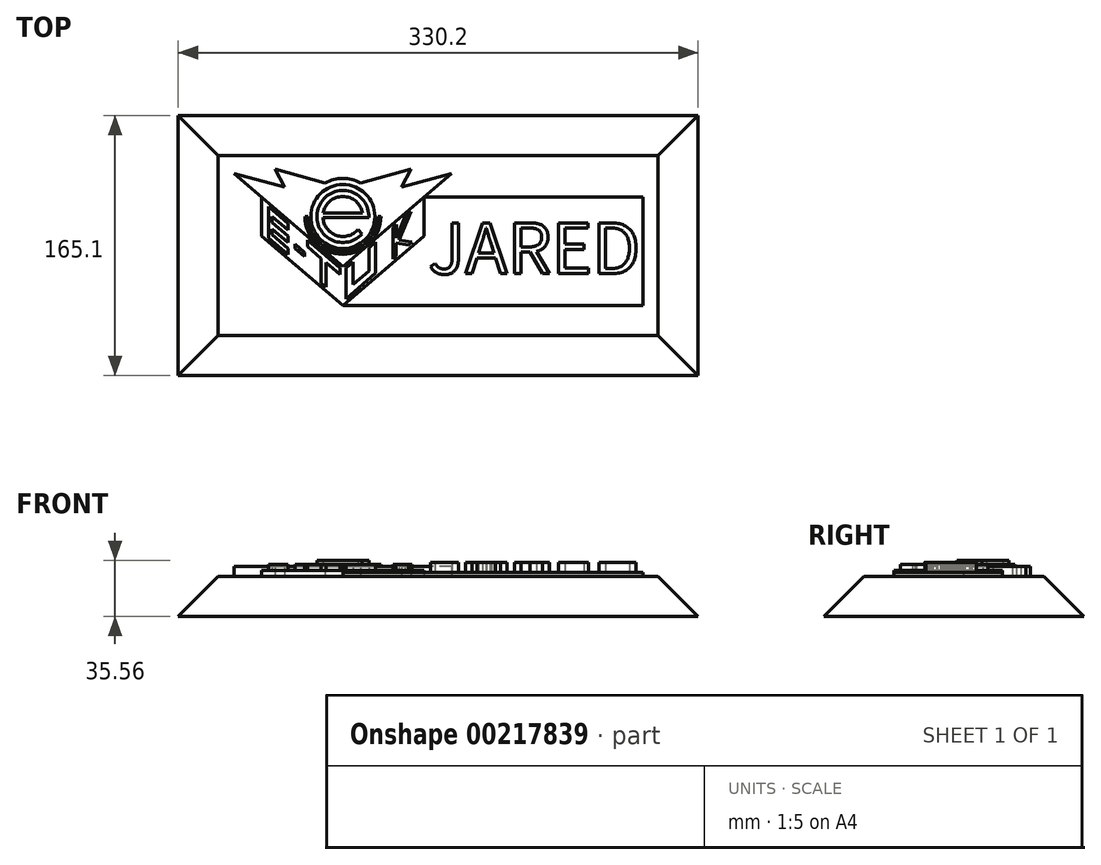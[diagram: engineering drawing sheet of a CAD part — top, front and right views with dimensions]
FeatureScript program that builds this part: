
annotation { "Feature Type Name" : "Feature", "Feature Type Description" : "" }
export const myFeature = defineFeature(function(context is Context, id is Id, definition is map)
    precondition{}
    {
        {
            var Q0;
            Q0=qCreatedBy(makeId("Top.planeOp"),FACE);
            var sketch = newSketch(context, id + "F0", { "sketchPlane" : qUnion([Q0])});
            skArc(sketch, "E0", {"start": v(12.53, 2.07) * mm, "mid": v(0, 12.7) * mm, "end": v(-12.53, 2.07) * mm});
            skArc(sketch, "E1", {"start": v(16.5, -0.78) * mm, "mid": v(-15.23, 6.37) * mm, "end": v(12.14, -11.18) * mm});
            skLineSegment(sketch, "E2", {"start": v(12.7, -0.78) * mm, "end": v(-12.68, -0.78) * mm});
            skLineSegment(sketch, "E3", {"start": v(-12.68, -0.78) * mm, "end": v(16.5, -0.78) * mm});
            skLineSegment(sketch, "E4", {"start": v(9.59, -8.33) * mm, "end": v(12.14, -11.18) * mm});
            skArc(sketch, "E5.trimOffspring", {"start": v(-12.68, -0.78) * mm, "mid": v(-4.08, -12.03) * mm, "end": v(9.59, -8.33) * mm});
            skLineSegment(sketch, "E6", {"start": v(-12.53, 2.07) * mm, "end": v(12.53, 2.07) * mm});
            skSolve(sketch);
        }
        {
            var Q0;
            Q0=makeQuery(id+"F0.imprint","IMPRINT",FACE,{"disambiguationData":[TD([[makeQuery(id+"F0.imprint","IMPRINT",EDGE,{"derivedFrom":sQuery(id+"F0.wireOp",EDGE,"E0")}),-1.0]])]});
            extrude(context, id + "F1", {"entities" : qUnion([Q0]), "depth" : 10.16 * mm});
        }
        {
            var Q0;
            Q0=qCreatedBy(makeId("Top.planeOp"),FACE);
            var sketch = newSketch(context, id + "F2", { "sketchPlane" : qUnion([Q0])});
            skCircle(sketch, "E7", {"center": v(0, 0) * mm, "radius": 20.32 * mm});
            skSolve(sketch);
        }
        {
            var Q0;
            Q0=qSketchRegion(id+"F2",true);
            extrude(context, id + "F3", {"entities" : qUnion([Q0]), "operationType" : NewBodyOperationType.ADD, "depth" : 7.62 * mm});
        }
        {
            var Q0;
            Q0=qCreatedBy(makeId("Top.planeOp"),FACE);
            var sketch = newSketch(context, id + "F4", { "sketchPlane" : qUnion([Q0])});
            skLineSegment(sketch, "E8", {"start": v(-69.02, 27.27) * mm, "end": v(-37.13, 18.72) * mm});
            skLineSegment(sketch, "E9", {"start": v(-37.13, 18.72) * mm, "end": v(-43.14, 30.14) * mm});
            skLineSegment(sketch, "E10", {"start": v(-43.14, 30.14) * mm, "end": v(-11.32, 21.31) * mm});
            skLineSegment(sketch, "E11", {"start": v(-69.02, 27.27) * mm, "end": v(0, -31.75) * mm});
            skLineSegment(sketch, "E12.MirrorCS", {"start": v(43.14, 30.14) * mm, "end": v(11.32, 21.31) * mm});
            skLineSegment(sketch, "E13.MirrorCS", {"start": v(69.02, 27.27) * mm, "end": v(0, -31.75) * mm});
            skLineSegment(sketch, "E14.MirrorCS", {"start": v(69.02, 27.27) * mm, "end": v(37.13, 18.72) * mm});
            skLineSegment(sketch, "E15.MirrorCS", {"start": v(37.13, 18.72) * mm, "end": v(43.14, 30.14) * mm});
            skArc(sketch, "E16.trimOffspring", {"start": v(11.32, 21.31) * mm, "mid": v(0, 24.13) * mm, "end": v(-11.32, 21.31) * mm});
            skSolve(sketch);
        }
        {
            var Q0;
            Q0=qSketchRegion(id+"F4",true);
            var Q1;
            Q1=makeQuery(id+"F2.imprint","IMPRINT",FACE,{"disambiguationData":[TD([[makeQuery(id+"F2.imprint","IMPRINT",EDGE,{"derivedFrom":sQuery(id+"F2.wireOp",EDGE,"E7")}),1.0]])]});
            extrude(context, id + "F5", {"entities" : qUnion([Q0, Q1]), "operationType" : NewBodyOperationType.ADD, "depth" : 6.35 * mm});
        }
        {
            var Q0;
            Q0=qCreatedBy(makeId("Top.planeOp"),FACE);
            var sketch = newSketch(context, id + "F6", { "sketchPlane" : qUnion([Q0])});
            skLineSegment(sketch, "E17", {"start": v(-51.6, -12.38) * mm, "end": v(0, -56.51) * mm});
            skLineSegment(sketch, "E18", {"start": v(0, -56.51) * mm, "end": v(51.6, -12.38) * mm});
            skLineSegment(sketch, "E19", {"start": v(-51.6, 12.38) * mm, "end": v(-51.6, -12.38) * mm});
            skLineSegment(sketch, "E20", {"start": v(51.6, 12.38) * mm, "end": v(51.6, -12.38) * mm});
            skLineSegment(sketch, "E21", {"start": v(-51.6, 12.38) * mm, "end": v(0, -31.75) * mm});
            skLineSegment(sketch, "E22", {"start": v(0, -31.75) * mm, "end": v(51.6, 12.38) * mm});
            skSolve(sketch);
        }
        {
            var Q0;
            Q0=qSketchRegion(id+"F6",true);
            extrude(context, id + "F7", {"entities" : qUnion([Q0]), "operationType" : NewBodyOperationType.ADD, "depth" : 3.8 * mm});
        }
        {
            var Q0;
            Q0=makeQuery(id+"F7.opExtrude","CAP_FACE",FACE,{"disambiguationData":[OSD([sQuery(id+"F6.wireOp",EDGE,"E17"),sQuery(id+"F6.wireOp",EDGE,"E18"),sQuery(id+"F6.wireOp",EDGE,"E19"),sQuery(id+"F6.wireOp",EDGE,"E20"),sQuery(id+"F6.wireOp",EDGE,"E21"),sQuery(id+"F6.wireOp",EDGE,"E22")])],"isStart":false});
            var sketch = newSketch(context, id + "F8", { "sketchPlane" : qUnion([Q0])});
            skPoint(sketch, "E23.startSnap0", {"position": v(-51.6, 0) * mm});
            skLineSegment(sketch, "E24", {"start": v(-51.6, -9.87) * mm, "end": v(-51.6, 9.87) * mm, "construction": true});
            skLineSegment(sketch, "E25", {"start": v(-47.26, 6.16) * mm, "end": v(-34.74, -4.55) * mm});
            skLineSegment(sketch, "E26", {"start": v(-34.74, -4.55) * mm, "end": v(-34.74, -8.63) * mm});
            skLineSegment(sketch, "E27", {"start": v(-34.74, -8.63) * mm, "end": v(-44.83, 0) * mm});
            skLineSegment(sketch, "E28", {"start": v(-44.83, 0) * mm, "end": v(-44.83, -3.75) * mm});
            skLineSegment(sketch, "E29", {"start": v(-44.83, -3.75) * mm, "end": v(-34.74, -12.38) * mm});
            skLineSegment(sketch, "E30", {"start": v(-34.74, -12.38) * mm, "end": v(-34.74, -16.46) * mm});
            skLineSegment(sketch, "E31", {"start": v(-34.74, -16.46) * mm, "end": v(-44.83, -7.83) * mm});
            skLineSegment(sketch, "E32", {"start": v(-44.83, -7.83) * mm, "end": v(-44.83, -11.58) * mm});
            skLineSegment(sketch, "E33", {"start": v(-44.83, -11.58) * mm, "end": v(-34.74, -20.21) * mm});
            skLineSegment(sketch, "E34", {"start": v(-34.74, -20.21) * mm, "end": v(-34.74, -24.3) * mm});
            skLineSegment(sketch, "E35", {"start": v(-34.74, -24.3) * mm, "end": v(-47.26, -13.59) * mm});
            skLineSegment(sketch, "E36", {"start": v(-47.26, 6.16) * mm, "end": v(-47.26, -13.59) * mm});
            skLineSegment(sketch, "E37", {"start": v(-30.38, -20.21) * mm, "end": v(-30.38, -17.65) * mm});
            skLineSegment(sketch, "E38", {"start": v(-30.38, -17.65) * mm, "end": v(-24.17, -22.96) * mm});
            skLineSegment(sketch, "E39", {"start": v(-24.17, -22.96) * mm, "end": v(-24.17, -25.53) * mm});
            skLineSegment(sketch, "E40", {"start": v(-24.17, -25.53) * mm, "end": v(-30.38, -20.21) * mm});
            skLineSegment(sketch, "E41", {"start": v(-22.38, -15.12) * mm, "end": v(-1.9, -32.63) * mm});
            skLineSegment(sketch, "E42", {"start": v(-1.9, -32.63) * mm, "end": v(-1.9, -36.71) * mm});
            skLineSegment(sketch, "E43", {"start": v(-1.9, -36.71) * mm, "end": v(-10.6, -29.28) * mm});
            skLineSegment(sketch, "E44", {"start": v(-10.6, -29.28) * mm, "end": v(-10.6, -44.95) * mm});
            skLineSegment(sketch, "E45", {"start": v(-10.6, -44.95) * mm, "end": v(-13.7, -42.3) * mm});
            skLineSegment(sketch, "E46", {"start": v(-13.7, -42.3) * mm, "end": v(-13.7, -26.63) * mm});
            skLineSegment(sketch, "E47", {"start": v(-13.7, -26.63) * mm, "end": v(-22.38, -19.2) * mm});
            skLineSegment(sketch, "E48", {"start": v(-22.38, -19.2) * mm, "end": v(-22.38, -15.12) * mm});
            skLineSegment(sketch, "E49", {"start": v(1.9, -32.62) * mm, "end": v(6.3, -28.86) * mm});
            skLineSegment(sketch, "E50", {"start": v(6.3, -28.86) * mm, "end": v(6.3, -43.26) * mm});
            skLineSegment(sketch, "E51", {"start": v(6.3, -43.26) * mm, "end": v(16.5, -34.54) * mm});
            skLineSegment(sketch, "E52", {"start": v(16.5, -34.54) * mm, "end": v(16.5, -20.14) * mm});
            skLineSegment(sketch, "E53", {"start": v(16.5, -20.14) * mm, "end": v(20.85, -16.3) * mm});
            skLineSegment(sketch, "E54", {"start": v(20.85, -16.3) * mm, "end": v(20.85, -36.06) * mm});
            skLineSegment(sketch, "E55", {"start": v(20.85, -36.06) * mm, "end": v(1.9, -52.37) * mm});
            skLineSegment(sketch, "E56", {"start": v(1.9, -52.37) * mm, "end": v(1.9, -32.62) * mm});
            skLineSegment(sketch, "E57", {"start": v(31.73, -7.12) * mm, "end": v(31.73, -27.15) * mm});
            skLineSegment(sketch, "E58", {"start": v(31.73, -27.15) * mm, "end": v(33.91, -25.22) * mm});
            skLineSegment(sketch, "E59", {"start": v(33.91, -25.22) * mm, "end": v(33.91, -16.82) * mm});
            skLineSegment(sketch, "E60", {"start": v(33.94, -13.64) * mm, "end": v(33.94, -5.23) * mm});
            skLineSegment(sketch, "E61", {"start": v(33.94, -5.23) * mm, "end": v(31.73, -7.12) * mm});
            skLineSegment(sketch, "E62", {"start": v(41.79, -18.27) * mm, "end": v(44, -16.38) * mm});
            skLineSegment(sketch, "E63", {"start": v(33.94, -13.64) * mm, "end": v(39.5, 0) * mm});
            skLineSegment(sketch, "E64", {"start": v(33.91, -16.82) * mm, "end": v(41.79, -18.27) * mm});
            skLineSegment(sketch, "E65", {"start": v(44, -16.38) * mm, "end": v(35.85, -14.87) * mm});
            skLineSegment(sketch, "E66", {"start": v(35.85, -14.87) * mm, "end": v(43.2, 3.16) * mm});
            skLineSegment(sketch, "E67", {"start": v(39.5, 0) * mm, "end": v(43.2, 3.16) * mm});
            skSolve(sketch);
        }
        {
            var Q0;
            Q0=qSketchRegion(id+"F8",true);
            extrude(context, id + "F9", {"entities" : qUnion([Q0]), "operationType" : NewBodyOperationType.ADD, "depth" : 3.8 * mm});
        }
        {
            var Q0;
            Q0=makeQuery(id+"F5.boolean.opBoolean","MERGE",FACE,{"derivedFrom":[makeQuery(id+"F5.opExtrude","CAP_FACE",FACE,{"disambiguationData":[OSD([sQuery(id+"F2.wireOp",EDGE,"E7")])],"isStart":false}),makeQuery(id+"F5.opExtrude","CAP_FACE",FACE,{"disambiguationData":[OSD([sQuery(id+"F4.wireOp",EDGE,"E8"),sQuery(id+"F4.wireOp",EDGE,"E9"),sQuery(id+"F4.wireOp",EDGE,"E10"),sQuery(id+"F4.wireOp",EDGE,"E11"),sQuery(id+"F4.wireOp",EDGE,"E13.MirrorCS"),sQuery(id+"F4.wireOp",EDGE,"E14.MirrorCS"),sQuery(id+"F4.wireOp",EDGE,"E12.MirrorCS"),sQuery(id+"F4.wireOp",EDGE,"E15.MirrorCS"),sQuery(id+"F4.wireOp",EDGE,"E16.trimOffspring")])],"isStart":false})]});
            var sketch = newSketch(context, id + "F10", { "sketchPlane" : qUnion([Q0])});
            skArc(sketch, "E68", {"start": v(-24.13, 0) * mm, "mid": v(0, -24.13) * mm, "end": v(24.13, 0) * mm});
            skArc(sketch, "E69", {"start": v(-22.23, 0) * mm, "mid": v(0, -22.23) * mm, "end": v(22.23, 0) * mm});
            skLineSegment(sketch, "E70", {"start": v(-24.13, 0) * mm, "end": v(-22.23, 0) * mm});
            skLineSegment(sketch, "E71", {"start": v(24.13, 0) * mm, "end": v(22.23, 0) * mm});
            skSolve(sketch);
        }
        {
            var Q0;
            Q0=qSketchRegion(id+"F10",true);
            extrude(context, id + "F11", {"entities" : qUnion([Q0]), "operationType" : NewBodyOperationType.ADD, "depth" : 1.27 * mm});
        }
        {
            var Q0;
            {var subQ0=sQuery(id+"F2.wireOp",EDGE,"E7");Q0=makeQuery(id+"F7.boolean.opBoolean","MERGE",FACE,{"derivedFrom":[makeQuery(id+"F5.boolean.opBoolean","MERGE",FACE,{"derivedFrom":[makeQuery(id+"F3.boolean.opBoolean","MERGE",FACE,{"derivedFrom":[makeQuery(id+"F1.opExtrude","CAP_FACE",FACE,{"disambiguationData":[OSD([sQuery(id+"F0.wireOp",EDGE,"E0"),sQuery(id+"F0.wireOp",EDGE,"E1"),sQuery(id+"F0.wireOp",EDGE,"E3"),sQuery(id+"F0.wireOp",EDGE,"E4"),sQuery(id+"F0.wireOp",EDGE,"E5.trimOffspring"),sQuery(id+"F0.wireOp",EDGE,"E6")])],"isStart":true}),makeQuery(id+"F3.opExtrude","CAP_FACE",FACE,{"disambiguationData":[OSD([subQ0])],"isStart":true})]}),makeQuery(id+"F5.opExtrude","CAP_FACE",FACE,{"disambiguationData":[OSD([subQ0])],"isStart":true}),makeQuery(id+"F5.opExtrude","CAP_FACE",FACE,{"disambiguationData":[OSD([sQuery(id+"F4.wireOp",EDGE,"E8"),sQuery(id+"F4.wireOp",EDGE,"E9"),sQuery(id+"F4.wireOp",EDGE,"E10"),sQuery(id+"F4.wireOp",EDGE,"E11"),sQuery(id+"F4.wireOp",EDGE,"E13.MirrorCS"),sQuery(id+"F4.wireOp",EDGE,"E14.MirrorCS"),sQuery(id+"F4.wireOp",EDGE,"E12.MirrorCS"),sQuery(id+"F4.wireOp",EDGE,"E15.MirrorCS"),sQuery(id+"F4.wireOp",EDGE,"E16.trimOffspring")])],"isStart":true})]}),makeQuery(id+"F7.opExtrude","CAP_FACE",FACE,{"disambiguationData":[OSD([sQuery(id+"F6.wireOp",EDGE,"E17"),sQuery(id+"F6.wireOp",EDGE,"E18"),sQuery(id+"F6.wireOp",EDGE,"E19"),sQuery(id+"F6.wireOp",EDGE,"E20"),sQuery(id+"F6.wireOp",EDGE,"E21"),sQuery(id+"F6.wireOp",EDGE,"E22")])],"isStart":true})]});}
            var sketch = newSketch(context, id + "F12", { "sketchPlane" : qUnion([Q0])});
            skLineSegment(sketch, "E72.bottom", {"start": v(0, 56.51) * mm, "end": v(190.5, 56.51) * mm});
            skLineSegment(sketch, "E72.right", {"start": v(190.5, 56.51) * mm, "end": v(190.5, -12.38) * mm});
            skLineSegment(sketch, "E73", {"start": v(51.6, -12.38) * mm, "end": v(190.5, -12.38) * mm});
            skLineSegment(sketch, "E74", {"start": v(0, 56.51) * mm, "end": v(51.6, 12.38) * mm});
            skLineSegment(sketch, "E75", {"start": v(51.6, 12.38) * mm, "end": v(51.6, -12.38) * mm});
            skSolve(sketch);
        }
        {
            var Q0;
            Q0=qSketchRegion(id+"F12",true);
            extrude(context, id + "F13", {"entities" : qUnion([Q0]), "operationType" : NewBodyOperationType.ADD, "oppositeDirection" : true, "depth" : 2.54 * mm});
        }
        {
            var Q0;
            Q0=makeQuery(id+"F13.opExtrude","CAP_FACE",FACE,{"disambiguationData":[OSD([sQuery(id+"F12.wireOp",EDGE,"E72.bottom"),sQuery(id+"F12.wireOp",EDGE,"E72.right"),sQuery(id+"F12.wireOp",EDGE,"E73"),sQuery(id+"F12.wireOp",EDGE,"E74"),sQuery(id+"F12.wireOp",EDGE,"E75")])],"isStart":false});
            var sketch = newSketch(context, id + "F14", { "sketchPlane" : qUnion([Q0])});
            skLineSegment(sketch, "E76", {"start": v(51.6, 12.38) * mm, "end": v(51.6, -56.51) * mm, "construction": true});
            skLineSegment(sketch, "E77", {"start": v(51.6, -56.51) * mm, "end": v(190.5, -56.51) * mm, "construction": true});
            skLineSegment(sketch, "E78", {"start": v(190.5, -56.51) * mm, "end": v(190.5, 12.38) * mm, "construction": true});
            skLineSegment(sketch, "E79", {"start": v(190.5, 12.38) * mm, "end": v(51.6, 12.38) * mm, "construction": true});
            skPoint(sketch, "E80.startSnap0", {"position": v(51.6, 0) * mm});
            skPoint(sketch, "E80.endSnap0", {"position": v(51.6, 0) * mm});
            skLineSegment(sketch, "E81", {"start": v(188.69, -36.36) * mm, "end": v(54.1, -36.36) * mm, "construction": true});
            skLineSegment(sketch, "E82", {"start": v(178.12, -4.6) * mm, "end": v(54.1, -4.6) * mm, "construction": true});
            skText(sketch, "E83", { "text": "JARED", "fontName": "NotoSansCJKkr-Regular.otf"});
            const initialGuessF14  = {"E83": [0.0541, -0.03636, 1, 0, 0.03175]};
            skSetInitialGuess(sketch, initialGuessF14);
            skSolve(sketch);
        }
        {
            var Q0;
            Q0 = qSketchRegion(id + "F14", true);
            extrude(context, id + "F15", {"entities" : qUnion([Q0]), "operationType" : NewBodyOperationType.ADD, "depth" : 6.35 * mm});
        }
        {
            var Q0;
            Q0=makeQuery(id+"F13.opExtrude","CAP_FACE",FACE,{"disambiguationData":[OSD([sQuery(id+"F12.wireOp",EDGE,"E72.bottom"),sQuery(id+"F12.wireOp",EDGE,"E72.right"),sQuery(id+"F12.wireOp",EDGE,"E73"),sQuery(id+"F12.wireOp",EDGE,"E74"),sQuery(id+"F12.wireOp",EDGE,"E75")])],"isStart":true});
            var sketch = newSketch(context, id + "F16", { "sketchPlane" : qUnion([Q0])});
            skLineSegment(sketch, "E84.bottom", {"start": v(-79.18, -38.74) * mm, "end": v(200.22, -38.74) * mm});
            skLineSegment(sketch, "E84.top", {"start": v(-79.18, 75.56) * mm, "end": v(200.22, 75.56) * mm});
            skLineSegment(sketch, "E84.left", {"start": v(-79.18, -38.74) * mm, "end": v(-79.18, 75.56) * mm});
            skLineSegment(sketch, "E84.right", {"start": v(200.22, -38.74) * mm, "end": v(200.22, 75.56) * mm});
            skSolve(sketch);
        }
        {
            var Q0;
            Q0 = qSketchRegion(id + "F16", true);
            extrude(context, id + "F17", {"entities" : qUnion([Q0]), "operationType" : NewBodyOperationType.ADD, "depth" : 25.4 * mm, "hasDraft" : true, "draftAngle" : 45 * degree});
        }
    });
